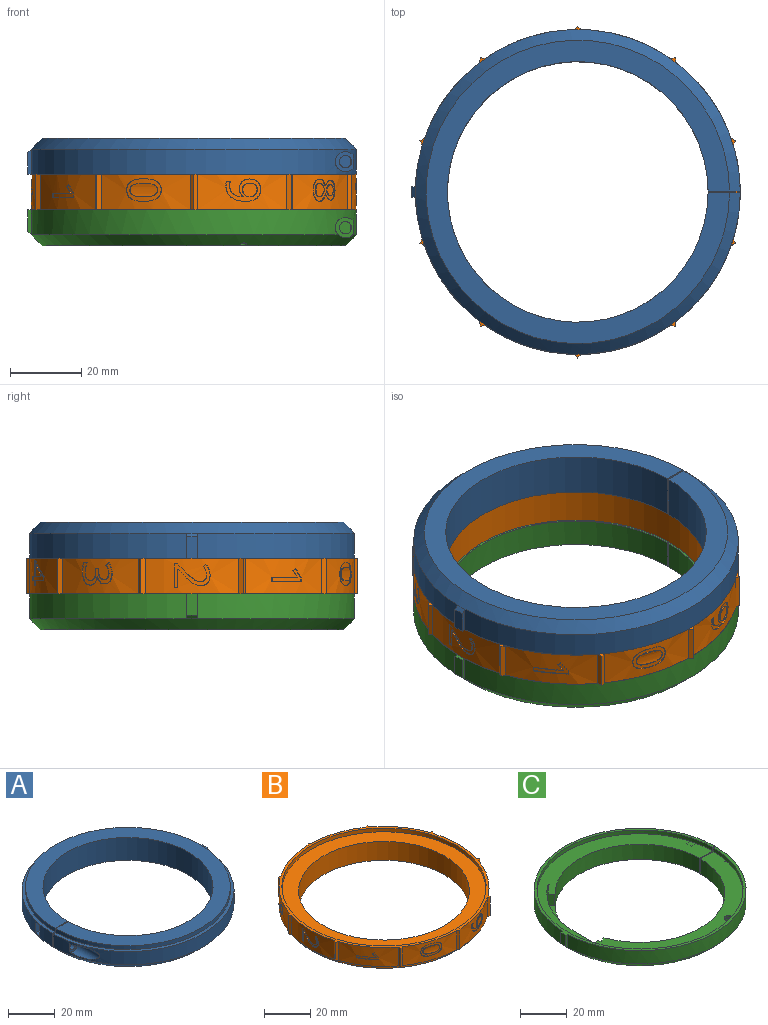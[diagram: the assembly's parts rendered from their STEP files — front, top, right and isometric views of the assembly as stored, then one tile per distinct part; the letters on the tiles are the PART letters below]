
ASSEMBLY  parts=3 mates=2
PART A: 26 faces, bbox 92x91x12 mm
  f0: plane 1.5x0.02mm, normal (0,0,-1), area 0mm2, adj f9,f23,f25
  f1: cylinder r=45.5mm len=90.97mm, axis (0,0,-1), area 970.8mm2, adj f5,f9,f11,f15,f16,f17,f18,f23
  f2: cylinder r=45.5mm len=90.97mm, axis (0,0,-1), area 920.2mm2, adj f5,f9,f10,f13,f14,f21
  f3: cylinder r=1.7mm len=8.75mm, axis (0,1,0), area 93.5mm2, adj f10,f14
  f4: cylinder r=36.5mm len=73mm, axis (0,0,-1), area 2746mm2, adj f6,f8,f10,f11
  f5: plane 92x91mm, normal (0,0,1), area 424mm2, adj f1,f2,f7,f10,f11,f21,f22,f23
  f6: plane 85x85mm, normal (0,0,-1), area 1486.1mm2, adj f4,f9,f10,f11
  f7: cylinder r=44mm len=88mm, axis (0,0,-1), area 551.9mm2, adj f5,f8,f10,f11
  f8: plane 88x88mm, normal (0,0,1), area 1893mm2, adj f4,f7,f10,f11
  f9: cone r=45.5mm half-angle=45deg, axis (0,0,1), area 1170.8mm2, adj f0,f1,f2,f6,f10,f11,f24
  f10: plane 12x9mm, normal (0,1,0), area 91.4mm2, adj f2,f3,f4,f5,f6,f7,f8,f9
  f11: plane 12x9mm, normal (0,-1,0), area 91.4mm2, adj f1,f4,f5,f6,f7,f8,f9,f12
  f12: cylinder r=1.7mm len=8.75mm, axis (0,1,0), area 93.5mm2, adj f11,f18
  f13: cylinder r=2.85mm len=13.32mm, axis (0,1,0), area 118.8mm2, adj f2,f14
  f14: plane 5.7x4.95mm, normal (0,-1,0), area 14.5mm2, adj f2,f3,f13
  f15: plane 3.75x3mm, normal (0,0,1), area 10.2mm2, adj f1,f17,f18,f19
  f16: plane 3.75x3mm, normal (0,0,-1), area 10.2mm2, adj f1,f17,f18,f20
  f17: plane 5.7x4.68mm, normal (0,-1,0), area 22mm2, adj f1,f15,f16,f19,f20
  f18: plane 5.7x5.39mm, normal (0,1,0), area 17mm2, adj f1,f12,f15,f16,f19,f20
  f19: plane 3x2.85mm, normal (-0.87,0,0.5), area 9.9mm2, adj f15,f17,f18,f20
  f20: plane 3x2.85mm, normal (-0.87,0,-0.5), area 9.9mm2, adj f16,f17,f18,f19
  f21: plane 7x1.02mm, normal (0,-1,0), area 6.7mm2, adj f2,f5,f22,f24,f25
  f22: plane 6x3mm, normal (1,0,0), area 18mm2, adj f5,f21,f23,f25
  f23: plane 7x1.02mm, normal (0,1,0), area 6.7mm2, adj f0,f1,f5,f22,f25
  f24: plane 1.5x0.02mm, normal (0,0,-1), area 0mm2, adj f9,f21,f25
  f25: plane 3x1mm, normal (0.71,0,-0.71), area 4.2mm2, adj f0,f21,f22,f23,f24
PART B: 250 faces, bbox 91x93x12 mm
  f0: cylinder r=1.5mm len=3mm, axis (0,0,-1), area 18.8mm2, adj f1,f32
  f1: plane 3x3mm, normal (0,0,-1), area 7.1mm2, adj f0
  f2: cylinder r=1.5mm len=3mm, axis (0,0,-1), area 18.8mm2, adj f3,f32
  f3: plane 3x3mm, normal (0,0,-1), area 7.1mm2, adj f2
  f4: cylinder r=1.5mm len=3mm, axis (0,0,-1), area 18.8mm2, adj f5,f32
  f5: plane 3x3mm, normal (0,0,-1), area 7.1mm2, adj f4
  f6: cylinder r=1.5mm len=3mm, axis (0,0,-1), area 18.8mm2, adj f7,f32
  f7: plane 3x3mm, normal (0,0,-1), area 7.1mm2, adj f6
  f8: cylinder r=1.5mm len=3mm, axis (0,0,-1), area 18.8mm2, adj f9,f32
  f9: plane 3x3mm, normal (0,0,-1), area 7.1mm2, adj f8
  f10: cylinder r=1.5mm len=3mm, axis (0,0,-1), area 18.8mm2, adj f11,f32
  f11: plane 3x3mm, normal (0,0,-1), area 7.1mm2, adj f10
  f12: cylinder r=1.5mm len=3mm, axis (0,0,-1), area 18.8mm2, adj f13,f32
  f13: plane 3x3mm, normal (0,0,-1), area 7.1mm2, adj f12
  f14: cylinder r=1.5mm len=3mm, axis (0,0,-1), area 18.8mm2, adj f15,f32
  f15: plane 3x3mm, normal (0,0,-1), area 7.1mm2, adj f14
  f16: cylinder r=1.5mm len=3mm, axis (0,0,-1), area 18.8mm2, adj f17,f32
  f17: plane 3x3mm, normal (0,0,-1), area 7.1mm2, adj f16
  f18: cylinder r=45.5mm len=26.21mm, axis (0,0,-1), area 247.6mm2, adj f29,f30,f220,f221,f222,f223,f224,f225
  f19: cylinder r=45.5mm len=21.21mm, axis (0,0,-1), area 225.9mm2, adj f29,f30,f201,f202,f203,f204,f205,f206
  f20: cylinder r=45.5mm len=24.93mm, axis (0,0,-1), area 243.7mm2, adj f29,f30,f178,f179,f180,f181,f182,f183
  f21: cylinder r=45.5mm len=24.93mm, axis (0,0,-1), area 231.8mm2, adj f29,f30,f162,f163,f164,f165,f166,f167
  f22: cylinder r=45.5mm len=21.21mm, axis (0,0,-1), area 242.3mm2, adj f29,f30,f135,f136,f137,f138,f139,f140
  f23: cylinder r=45.5mm len=26.21mm, axis (0,0,-1), area 244.2mm2, adj f29,f30,f114,f115,f116,f117,f118,f119
  f24: cylinder r=45.5mm len=21.21mm, axis (0,0,-1), area 251.4mm2, adj f29,f30,f104,f105,f106,f107,f108,f109
  f25: cylinder r=45.5mm len=24.93mm, axis (0,0,-1), area 214.8mm2, adj f29,f30,f93,f94,f95,f96,f100,f101
  f26: cylinder r=45.5mm len=21.21mm, axis (0,0,-1), area 223.1mm2, adj f29,f30,f67,f68,f69,f70,f71,f72
  f27: cylinder r=45.5mm len=24.93mm, axis (0,0,-1), area 225.9mm2, adj f29,f30,f40,f41,f42,f43,f44,f45
  f28: cylinder r=37mm len=74mm, axis (0,0,-1), area 2324.8mm2, adj f32,f34
  f29: plane 92.98x91mm, normal (0,0,1), area 362.3mm2, adj f18,f19,f20,f21,f22,f23,f24,f25
  f30: plane 92.98x91mm, normal (0,0,-1), area 431.6mm2, adj f18,f19,f20,f21,f22,f23,f24,f25
  f31: cylinder r=44mm len=88mm, axis (0,0,1), area 552.9mm2, adj f30,f32
  f32: plane 88x88mm, normal (0,0,-1), area 1710.6mm2, adj f0,f2,f4,f6,f8,f10,f12,f14
  f33: cylinder r=44.25mm len=88.5mm, axis (0,0,1), area 556.1mm2, adj f29,f34
  f34: plane 88.5x88.5mm, normal (0,0,1), area 1850.6mm2, adj f28,f33
  f35: extruded ~1.74x0.9mm, area 0.5mm2, adj f36,f53,f57,f58
  f36: extruded ~1.35x0.67mm, area 0.5mm2, adj f35,f37,f57,f58
  f37: extruded ~1.45x0.83mm, area 0.5mm2, adj f36,f38,f57,f58
  f38: extruded ~1.81x0.92mm, area 0.6mm2, adj f37,f39,f57,f58
  f39: extruded ~1.29x0.69mm, area 0.4mm2, adj f38,f52,f57,f58
  f40: extruded ~1.17x0.34mm, area 0.4mm2, adj f27,f41,f55,f57
  f41: extruded ~5.72x4.33mm, area 2.5mm2, adj f27,f40,f42,f57
  f42: extruded ~3.2x1.43mm, area 1mm2, adj f27,f41,f43,f57
  f43: extruded ~2.36x1.23mm, area 0.8mm2, adj f27,f42,f44,f57
  f44: extruded ~2.2x0.97mm, area 0.7mm2, adj f27,f43,f45,f57
  f45: extruded ~2.46x1.19mm, area 0.8mm2, adj f27,f44,f46,f57
  f46: extruded ~2.21x1mm, area 0.7mm2, adj f27,f45,f47,f57
  f47: extruded ~2.07x0.86mm, area 0.7mm2, adj f27,f46,f48,f57
  f48: extruded ~2.09x1.2mm, area 0.8mm2, adj f27,f47,f49,f57
  f49: plane 0.29x0.09mm, normal (0.95,0.31,0), area 0mm2, adj f27,f48,f50,f57
  f50: extruded ~3.01x1.33mm, area 1mm2, adj f27,f49,f51,f57
  f51: extruded ~2.28x1.03mm, area 0.8mm2, adj f27,f50,f56,f57
  f52: extruded ~1.45x0.62mm, area 0.5mm2, adj f39,f54,f57,f58
  f53: extruded ~1.54x0.78mm, area 0.5mm2, adj f35,f54,f57,f58
  f54: extruded ~1.33x0.6mm, area 0.4mm2, adj f52,f53,f57,f58
  f55: plane 1.13x0.51mm, normal (0,0,-1), area 0.3mm2, adj f27,f40,f56,f57
  f56: extruded ~1.13x0.35mm, area 0.3mm2, adj f27,f51,f55,f57
  f57: cylinder r=45.5mm len=9.7mm, axis (0,0,-1), area 26.6mm2, adj f35,f36,f37,f38,f39,f40,f41,f42
  f58: cylinder r=45.5mm len=4.07mm, axis (0,0,-1), area 12mm2, adj f35,f36,f37,f38,f39,f52,f53,f54
  f59: plane 0.26x0.22mm, normal (0.53,0.73,-0.43), area 0.1mm2, adj f60,f79,f85,f86
  f60: extruded ~1.45x0.94mm, area 0.4mm2, adj f59,f61,f85,f86
  f61: extruded ~1.05x0.88mm, area 0.3mm2, adj f60,f62,f85,f86
  f62: extruded ~1.2x1mm, area 0.3mm2, adj f61,f78,f85,f86
  f63: extruded ~1.26x0.85mm, area 0.4mm2, adj f64,f83,f85,f87
  f64: extruded ~1.01x0.85mm, area 0.3mm2, adj f63,f65,f85,f87
  f65: extruded ~1.03x0.87mm, area 0.3mm2, adj f64,f66,f85,f87
  f66: extruded ~1.14x0.46mm, area 0.3mm2, adj f65,f76,f85,f87
  f67: extruded ~2.16x1.78mm, area 0.8mm2, adj f26,f68,f81,f85
  f68: extruded ~1.64x1.34mm, area 0.5mm2, adj f26,f67,f69,f85
  f69: extruded ~2.02x0.71mm, area 0.5mm2, adj f26,f68,f70,f85
  f70: extruded ~2x0.71mm, area 0.5mm2, adj f26,f69,f71,f85
  f71: extruded ~1.63x1.33mm, area 0.5mm2, adj f26,f70,f72,f85
  f72: extruded ~2.22x1.74mm, area 0.8mm2, adj f26,f71,f73,f85
  f73: extruded ~2.34x1.91mm, area 0.9mm2, adj f26,f72,f74,f85
  f74: extruded ~1.82x1.48mm, area 0.6mm2, adj f26,f73,f75,f85
  f75: extruded ~2.29x0.76mm, area 0.6mm2, adj f26,f74,f77,f85
  f76: extruded ~1.17x0.46mm, area 0.3mm2, adj f66,f84,f85,f87
  f77: extruded ~2.26x0.8mm, area 0.6mm2, adj f26,f75,f82,f85
  f78: extruded ~1.43x0.53mm, area 0.4mm2, adj f62,f80,f85,f86
  f79: extruded ~1.97x1.72mm, area 0.7mm2, adj f59,f80,f85,f86
  f80: extruded ~1.87x1.53mm, area 0.7mm2, adj f78,f79,f85,f86
  f81: extruded ~2.34x2.09mm, area 0.9mm2, adj f26,f67,f82,f85
  f82: extruded ~1.83x1.48mm, area 0.6mm2, adj f26,f77,f81,f85
  f83: extruded ~1.71x1.57mm, area 0.7mm2, adj f63,f84,f85,f87
  f84: extruded ~1.03x0.87mm, area 0.3mm2, adj f76,f83,f85,f87
  f85: cylinder r=45.5mm len=8.25mm, axis (0,0,-1), area 30.7mm2, adj f59,f60,f61,f62,f63,f64,f65,f66
  f86: cylinder r=45.5mm len=3.8mm, axis (0,0,-1), area 10.9mm2, adj f59,f60,f61,f62,f78,f79,f80
  f87: cylinder r=45.5mm len=3.17mm, axis (0,0,-1), area 6.8mm2, adj f63,f64,f65,f66,f76,f83,f84
  f88: extruded ~1.44x1mm, area 0.5mm2, adj f89,f98,f102,f103
  f89: extruded ~3.07x1.3mm, area 0.8mm2, adj f88,f90,f102,f103
  f90: extruded ~3.05x1.29mm, area 0.8mm2, adj f89,f91,f102,f103
  f91: extruded ~1.44x1mm, area 0.5mm2, adj f90,f92,f102,f103
  f92: extruded ~1.46x1.01mm, area 0.5mm2, adj f91,f97,f102,f103
  f93: extruded ~5.03x3.18mm, area 1.7mm2, adj f25,f94,f100,f102
  f94: extruded ~3.73x1.56mm, area 1mm2, adj f25,f93,f95,f102
  f95: extruded ~2.38x1.37mm, area 0.7mm2, adj f25,f94,f96,f102
  f96: extruded ~5.02x3.16mm, area 1.7mm2, adj f25,f95,f101,f102
  f97: extruded ~3.05x1.29mm, area 0.8mm2, adj f92,f99,f102,f103
  f98: extruded ~1.46x1.01mm, area 0.5mm2, adj f88,f99,f102,f103
  f99: extruded ~3.06x1.3mm, area 0.8mm2, adj f97,f98,f102,f103
  f100: extruded ~2.35x1.37mm, area 0.7mm2, adj f25,f93,f101,f102
  f101: extruded ~3.74x1.56mm, area 1mm2, adj f25,f96,f100,f102
  f102: cylinder r=45.5mm len=9.71mm, axis (0,0,-1), area 27.5mm2, adj f88,f89,f90,f91,f92,f93,f94,f95
  f103: cylinder r=45.5mm len=7.7mm, axis (0,0,-1), area 23.7mm2, adj f88,f89,f90,f91,f92,f97,f98,f99
  f104: plane 1.19x0.2mm, normal (0.59,-0.81,0), area 0.3mm2, adj f24,f105,f111,f113
  f105: plane 8.17x6.02mm, normal (0,0,1), area 2.5mm2, adj f24,f104,f106,f113
  f106: plane 1.02x0.2mm, normal (-0.59,0.81,0), area 0.3mm2, adj f24,f105,f112,f113
  f107: plane 0.79x0.73mm, normal (0.36,-0.5,-0.79), area 0.3mm2, adj f24,f108,f112,f113
  f108: plane 1x0.78mm, normal (0.45,-0.63,0.63), area 0.3mm2, adj f24,f107,f109,f113
  f109: extruded ~0.82x0.8mm, area 0.3mm2, adj f24,f108,f110,f113
  f110: extruded ~2.2x1.75mm, area 0.6mm2, adj f24,f109,f111,f113
  f111: plane 5.31x3.63mm, normal (0,0,-1), area 1.5mm2, adj f24,f104,f110,f113
  f112: plane 2.6x1.69mm, normal (-0.46,0.64,-0.62), area 0.8mm2, adj f24,f106,f107,f113
  f113: cylinder r=45.5mm len=8.03mm, axis (0,0,-1), area 14.5mm2, adj f104,f105,f106,f107,f108,f109,f110,f111
  f114: plane 1.04x0.35mm, normal (0,0,1), area 0.3mm2, adj f23,f115,f132,f134
  f115: plane 5.1x0.25mm, normal (0,1,0), area 1.3mm2, adj f23,f114,f116,f134
  f116: plane 0.25x0.05mm, normal (0,0,1), area 0mm2, adj f23,f115,f117,f134
  f117: plane 2.17x2.12mm, normal (0,-0.71,0.7), area 0.8mm2, adj f23,f116,f118,f134
  f118: extruded ~2.33x1.98mm, area 0.8mm2, adj f23,f117,f119,f134
  f119: extruded ~1.87x0.53mm, area 0.5mm2, adj f23,f118,f120,f134
  f120: extruded ~1.92x0.79mm, area 0.5mm2, adj f23,f119,f121,f134
  f121: extruded ~2.19x0.72mm, area 0.6mm2, adj f23,f120,f122,f134
  f122: extruded ~2.98x1.14mm, area 0.8mm2, adj f23,f121,f123,f134
  f123: plane 0.77x0.6mm, normal (0,-0.61,-0.79), area 0.2mm2, adj f23,f122,f124,f134
  f124: extruded ~1.23x0.74mm, area 0.4mm2, adj f23,f123,f125,f134
  f125: extruded ~1.17x0.27mm, area 0.3mm2, adj f23,f124,f126,f134
  f126: extruded ~1.34x0.46mm, area 0.4mm2, adj f23,f125,f127,f134
  f127: extruded ~1.26x0.48mm, area 0.3mm2, adj f23,f126,f128,f134
  f128: extruded ~1.05x0.29mm, area 0.3mm2, adj f23,f127,f129,f134
  f129: extruded ~1x0.57mm, area 0.3mm2, adj f23,f128,f130,f134
  f130: extruded ~1.72x1.57mm, area 0.6mm2, adj f23,f129,f131,f134
  f131: plane 2.63x2.61mm, normal (0,0.71,-0.71), area 0.9mm2, adj f23,f130,f133,f134
  f132: plane 6.52x0.25mm, normal (0,-1,0), area 1.6mm2, adj f23,f114,f133,f134
  f133: plane 0.97x0.35mm, normal (0,0,-1), area 0.2mm2, adj f23,f131,f132,f134
  f134: cylinder r=45.5mm len=10.06mm, axis (0,0,-1), area 21.7mm2, adj f114,f115,f116,f117,f118,f119,f120,f121
  f135: extruded ~1.59x0.81mm, area 0.5mm2, adj f22,f136,f156,f158
  f136: extruded ~1.45x1.17mm, area 0.4mm2, adj f22,f135,f137,f158
  f137: extruded ~1.68x1.37mm, area 0.5mm2, adj f22,f136,f138,f158
  f138: extruded ~2.18x0.73mm, area 0.6mm2, adj f22,f137,f139,f158
  f139: extruded ~2.96x1.03mm, area 0.8mm2, adj f22,f138,f140,f158
  f140: plane 0.87x0.65mm, normal (-0.35,-0.48,-0.81), area 0.3mm2, adj f22,f139,f141,f158
  f141: extruded ~2.33x0.85mm, area 0.6mm2, adj f22,f140,f142,f158
  f142: extruded ~1.23x0.49mm, area 0.3mm2, adj f22,f141,f143,f158
  f143: extruded ~1.08x0.91mm, area 0.3mm2, adj f22,f142,f144,f158
  f144: extruded ~1.28x1.05mm, area 0.4mm2, adj f22,f143,f145,f158
  f145: extruded ~1.68x0.57mm, area 0.4mm2, adj f22,f144,f146,f158
  f146: plane 0.9x0.2mm, normal (0.59,0.81,0), area 0.2mm2, adj f22,f145,f147,f158
  f147: plane 0.98x0.8mm, normal (0,0,-1), area 0.3mm2, adj f22,f146,f148,f158
  f148: plane 0.9x0.2mm, normal (-0.59,-0.81,0), area 0.2mm2, adj f22,f147,f149,f158
  f149: extruded ~2.58x1.59mm, area 0.9mm2, adj f22,f148,f150,f158
  f150: extruded ~2.4x1.81mm, area 0.9mm2, adj f22,f149,f151,f158
  f151: extruded ~2.6x0.71mm, area 0.7mm2, adj f22,f150,f152,f158
  f152: plane 1.02x0.96mm, normal (0,0,-1), area 0.3mm2, adj f22,f151,f153,f158
  f153: extruded ~2.63x0.61mm, area 0.7mm2, adj f22,f152,f154,f158
  f154: extruded ~2.71x0.84mm, area 0.7mm2, adj f22,f153,f155,f158
  f155: extruded ~1.99x1.6mm, area 0.6mm2, adj f22,f154,f157,f158
  f156: plane 0.23x0.18mm, normal (0,0,1), area 0mm2, adj f22,f135,f157,f158
  f157: extruded ~2.45x2.09mm, area 0.9mm2, adj f22,f155,f156,f158
  f158: cylinder r=45.5mm len=8.24mm, axis (0,0,-1), area 23.6mm2, adj f135,f136,f137,f138,f139,f140,f141,f142
  f159: plane 3.37x0.24mm, normal (0.95,0.31,0), area 0.8mm2, adj f160,f172,f176,f177
  f160: plane 3.99x2.79mm, normal (-0.53,-0.17,0.83), area 1.2mm2, adj f159,f161,f176,f177
  f161: extruded ~1.26x0.69mm, area 0.3mm2, adj f160,f171,f176,f177
  f162: plane 1.17x0.53mm, normal (0,0,1), area 0.3mm2, adj f21,f163,f174,f176
  f163: plane 1.45x0.24mm, normal (0.95,0.31,0), area 0.4mm2, adj f21,f162,f164,f176
  f164: plane 6.3x2.51mm, normal (0,0,1), area 1.7mm2, adj f21,f163,f165,f176
  f165: plane 1.27x0.24mm, normal (0.95,0.31,0), area 0.3mm2, adj f21,f164,f166,f176
  f166: plane 6.35x4.51mm, normal (0.53,0.17,-0.83), area 2mm2, adj f21,f165,f167,f176
  f167: plane 1.12x0.52mm, normal (0,0,-1), area 0.3mm2, adj f21,f166,f168,f176
  f168: plane 4.58x0.24mm, normal (-0.95,-0.31,0), area 1.1mm2, adj f21,f167,f169,f176
  f169: plane 2.25x0.74mm, normal (0,0,-1), area 0.6mm2, adj f21,f168,f170,f176
  f170: plane 1.19x0.24mm, normal (-0.95,-0.31,0), area 0.3mm2, adj f21,f169,f175,f176
  f171: plane 0.24x0.08mm, normal (-0.95,-0.31,0), area 0mm2, adj f161,f173,f176,f177
  f172: plane 2.38x0.96mm, normal (0,0,-1), area 0.6mm2, adj f159,f173,f176,f177
  f173: extruded ~2.91x1.28mm, area 0.7mm2, adj f171,f172,f176,f177
  f174: plane 1.45x0.24mm, normal (-0.95,-0.31,0), area 0.4mm2, adj f21,f162,f175,f176
  f175: plane 2.25x0.74mm, normal (0,0,1), area 0.6mm2, adj f21,f170,f174,f176
  f176: cylinder r=45.5mm len=9.48mm, axis (0,0,-1), area 25.5mm2, adj f159,f160,f161,f162,f163,f164,f165,f166
  f177: cylinder r=45.5mm len=5.04mm, axis (0,0,-1), area 8.6mm2, adj f159,f160,f161,f171,f172,f173
  f178: extruded ~2.41x0.61mm, area 0.6mm2, adj f20,f179,f193,f195
  f179: extruded ~2.64x0.93mm, area 0.7mm2, adj f20,f178,f180,f195
  f180: extruded ~2.46x1.15mm, area 0.7mm2, adj f20,f179,f181,f195
  f181: extruded ~2.11x0.93mm, area 0.6mm2, adj f20,f180,f182,f195
  f182: extruded ~2.3x0.82mm, area 0.6mm2, adj f20,f181,f183,f195
  f183: extruded ~1.42x0.28mm, area 0.4mm2, adj f20,f182,f184,f195
  f184: plane 2.82x0.97mm, normal (-0.09,0.03,1), area 0.7mm2, adj f20,f183,f185,f195
  f185: plane 3.61x0.24mm, normal (-0.95,0.31,0), area 0.9mm2, adj f20,f184,f186,f195
  f186: plane 1.18x0.48mm, normal (0,0,1), area 0.3mm2, adj f20,f185,f187,f195
  f187: plane 4.68x0.24mm, normal (0.95,-0.31,0), area 1.2mm2, adj f20,f186,f188,f195
  f188: plane 4.6x1.43mm, normal (0.08,-0.02,-1), area 1.2mm2, adj f20,f187,f189,f195
  f189: plane 0.61x0.44mm, normal (-0.8,0.26,-0.53), area 0.2mm2, adj f20,f188,f190,f195
  f190: extruded ~1.57x0.29mm, area 0.4mm2, adj f20,f189,f191,f195
  f191: extruded ~2.33x1.99mm, area 0.9mm2, adj f20,f190,f192,f195
  f192: extruded ~2.28x2.15mm, area 0.9mm2, adj f20,f191,f194,f195
  f193: plane 1.16x0.7mm, normal (0,0,-1), area 0.3mm2, adj f20,f178,f194,f195
  f194: extruded ~2.44x0.71mm, area 0.6mm2, adj f20,f192,f193,f195
  f195: cylinder r=45.5mm len=9.55mm, axis (0,0,-1), area 22.2mm2, adj f178,f179,f180,f181,f182,f183,f184,f185
  f196: extruded ~1.58x1.28mm, area 0.4mm2, adj f197,f214,f218,f219
  f197: extruded ~1.35x0.66mm, area 0.4mm2, adj f196,f198,f218,f219
  f198: extruded ~1.44x0.79mm, area 0.4mm2, adj f197,f199,f218,f219
  f199: extruded ~1.64x1.33mm, area 0.5mm2, adj f198,f200,f218,f219
  f200: extruded ~1.18x0.96mm, area 0.4mm2, adj f199,f213,f218,f219
  f201: extruded ~1.17x0.29mm, area 0.3mm2, adj f19,f202,f216,f218
  f202: extruded ~5.02x4.33mm, area 2.1mm2, adj f19,f201,f203,f218
  f203: extruded ~2.86x2.24mm, area 0.9mm2, adj f19,f202,f204,f218
  f204: extruded ~2.36x1.14mm, area 0.7mm2, adj f19,f203,f205,f218
  f205: extruded ~2.19x0.92mm, area 0.6mm2, adj f19,f204,f206,f218
  f206: extruded ~2.22x1.77mm, area 0.7mm2, adj f19,f205,f207,f218
  f207: extruded ~1.95x1.53mm, area 0.6mm2, adj f19,f206,f208,f218
  f208: extruded ~2.07x0.81mm, area 0.6mm2, adj f19,f207,f209,f218
  f209: extruded ~2.08x1.09mm, area 0.6mm2, adj f19,f208,f210,f218
  f210: plane 0.2x0.15mm, normal (0.59,-0.81,0), area 0mm2, adj f19,f209,f211,f218
  f211: extruded ~2.66x2.07mm, area 0.8mm2, adj f19,f210,f212,f218
  f212: extruded ~2.28x0.97mm, area 0.6mm2, adj f19,f211,f217,f218
  f213: extruded ~1.44x0.59mm, area 0.4mm2, adj f200,f215,f218,f219
  f214: extruded ~1.39x1.12mm, area 0.4mm2, adj f196,f215,f218,f219
  f215: extruded ~1.33x0.58mm, area 0.4mm2, adj f213,f214,f218,f219
  f216: plane 0.94x0.9mm, normal (0,0,1), area 0.3mm2, adj f19,f201,f217,f218
  f217: extruded ~1.13x0.31mm, area 0.3mm2, adj f19,f212,f216,f218
  f218: cylinder r=45.5mm len=8.25mm, axis (0,0,-1), area 26.7mm2, adj f196,f197,f198,f199,f200,f201,f202,f203
  f219: cylinder r=45.5mm len=3.82mm, axis (0,0,-1), area 12mm2, adj f196,f197,f198,f199,f200,f213,f214,f215
  f220: plane 1.32x0.25mm, normal (0,1,0), area 0.3mm2, adj f18,f221,f225,f227
  f221: plane 8.94x3.77mm, normal (0,0.39,0.92), area 2.4mm2, adj f18,f220,f226,f227
  f222: plane 6.37x0.25mm, normal (0,-1,0), area 1.6mm2, adj f18,f223,f226,f227
  f223: plane 1.13x0.36mm, normal (0,0,-1), area 0.3mm2, adj f18,f222,f224,f227
  f224: plane 5.11x0.25mm, normal (0,1,0), area 1.3mm2, adj f18,f223,f225,f227
  f225: plane 8.79x3.82mm, normal (0,-0.4,-0.92), area 2.4mm2, adj f18,f220,f224,f227
  f226: plane 0.98x0.35mm, normal (0,0,1), area 0.2mm2, adj f18,f221,f222,f227
  f227: cylinder r=45.5mm len=9.92mm, axis (0,0,-1), area 18.3mm2, adj f220,f221,f222,f223,f224,f225,f226
  f228: plane 10x1mm, normal (-0.71,0.71,0), area 14.1mm2, adj f21,f29,f30,f229
  f229: plane 10x1mm, normal (0.71,0.71,0), area 14.1mm2, adj f20,f29,f30,f228
  f230: plane 10x1.4mm, normal (-0.99,0.16,0), area 14.1mm2, adj f22,f29,f30,f231
  f231: plane 10x1.4mm, normal (0.16,0.99,0), area 14.1mm2, adj f21,f29,f30,f230
  f232: plane 10x1.26mm, normal (-0.89,-0.45,0), area 14.1mm2, adj f23,f29,f30,f233
  f233: plane 10x1.26mm, normal (-0.45,0.89,0), area 14.1mm2, adj f22,f29,f30,f232
  f234: plane 10x1.26mm, normal (-0.45,-0.89,0), area 14.1mm2, adj f24,f29,f30,f235
  f235: plane 10x1.26mm, normal (-0.89,0.45,0), area 14.1mm2, adj f23,f29,f30,f234
  f236: plane 10x1.4mm, normal (0.16,-0.99,0), area 14.1mm2, adj f25,f29,f30,f237
  f237: plane 10x1.4mm, normal (-0.99,-0.16,0), area 14.1mm2, adj f24,f29,f30,f236
  f238: plane 10x1mm, normal (0.71,-0.71,0), area 14.1mm2, adj f27,f29,f30,f239
  f239: plane 10x1mm, normal (-0.71,-0.71,0), area 14.1mm2, adj f25,f29,f30,f238
  f240: plane 10x1.4mm, normal (0.99,-0.16,0), area 14.1mm2, adj f26,f29,f30,f241
  f241: plane 10x1.4mm, normal (-0.16,-0.99,0), area 14.1mm2, adj f27,f29,f30,f240
  f242: plane 10x1.26mm, normal (0.89,0.45,0), area 14.1mm2, adj f18,f29,f30,f243
  f243: plane 10x1.26mm, normal (0.45,-0.89,0), area 14.1mm2, adj f26,f29,f30,f242
  f244: plane 10x1.26mm, normal (0.45,0.89,0), area 14.1mm2, adj f19,f29,f30,f245
  f245: plane 10x1.26mm, normal (0.89,-0.45,0), area 14.1mm2, adj f18,f29,f30,f244
  f246: plane 10x1.4mm, normal (-0.16,0.99,0), area 14.1mm2, adj f20,f29,f30,f247
  f247: plane 10x1.4mm, normal (0.99,0.16,0), area 14.1mm2, adj f19,f29,f30,f246
  f248: cylinder r=1.5mm len=3mm, axis (0,0,-1), area 18.8mm2, adj f32,f249
  f249: plane 3x3mm, normal (0,0,-1), area 7.1mm2, adj f248
PART C: 42 faces, bbox 92x91x10 mm
  f0: cylinder r=45.5mm len=90.97mm, axis (0,0,-1), area 974.7mm2, adj f1,f8,f26,f27,f32,f35,f40
  f1: cone r=45.5mm half-angle=45deg, axis (0,0,1), area 1155.1mm2, adj f0,f2,f3,f9,f22,f26,f27,f31
  f2: plane 1.5x0.02mm, normal (0,0,-1), area 0mm2, adj f1,f37,f39
  f3: cylinder r=45.5mm len=90.97mm, axis (0,0,-1), area 926.5mm2, adj f1,f8,f22,f23,f33,f37
  f4: plane 45.99x17.02mm, normal (0,0,1), area 159.5mm2, adj f5,f7,f12,f13,f14,f19,f20,f21
  f5: cylinder r=39.5mm len=6mm, axis (0,0,1), area 9.2mm2, adj f4,f6,f13,f34
  f6: plane 88.5x88.5mm, normal (0,0,1), area 1791.4mm2, adj f5,f7,f10,f12,f13,f14,f15,f19
  f7: cylinder r=36.5mm len=73mm, axis (0,0,-1), area 1586.4mm2, adj f4,f6,f9,f21,f32,f33,f34
  f8: plane 92x91mm, normal (0,0,1), area 354.8mm2, adj f0,f3,f10,f32,f33,f35,f36,f37
  f9: plane 85x85mm, normal (0,0,-1), area 1484.1mm2, adj f1,f7,f32,f33,f41
  f10: cylinder r=44.25mm len=88.5mm, axis (0,0,1), area 555.1mm2, adj f6,f8,f32,f33
  f11: cylinder r=1.7mm len=8.75mm, axis (0,-1,0), area 93.5mm2, adj f23,f33
  f12: plane 12x6mm, normal (1,0,0), area 72mm2, adj f4,f6,f13,f14
  f13: plane 6x2.37mm, normal (0,1,0), area 14.2mm2, adj f4,f5,f6,f12
  f14: cylinder r=40mm len=32.54mm, axis (0,0,1), area 228mm2, adj f4,f6,f12,f19
  f15: cylinder r=1.9mm len=3.8mm, axis (0,0,1), area 11.9mm2, adj f6,f16
  f16: plane 3.8x3.8mm, normal (0,0,1), area 3.8mm2, adj f15,f18
  f17: plane 3.1x3.1mm, normal (0,0,1), area 4.4mm2, adj f18,f41
  f18: cylinder r=1.55mm len=3.2mm, axis (0,0,1), area 31.2mm2, adj f16,f17
  f19: plane 6x0.41mm, normal (-0.81,-0.58,0), area 3mm2, adj f4,f6,f14,f20
  f20: cylinder r=39.5mm len=6mm, axis (0,0,1), area 43.1mm2, adj f4,f6,f19,f21
  f21: plane 6x2.16mm, normal (-0.69,-0.72,0), area 18mm2, adj f4,f6,f7,f20
  f22: cylinder r=2.85mm len=13.32mm, axis (0,1,0), area 110.8mm2, adj f1,f3,f23
  f23: plane 5.7x4.95mm, normal (0,-1,0), area 14.5mm2, adj f3,f11,f22
  f24: cylinder r=1.7mm len=8.75mm, axis (0,-1,0), area 93.5mm2, adj f27,f32
  f25: plane 3x0.42mm, normal (-0.87,0,-0.5), area 1.5mm2, adj f26,f27,f28,f40
  f26: plane 5.7x5.18mm, normal (0,-1,0), area 24.4mm2, adj f0,f1,f25,f28,f29,f30,f31
  f27: plane 5.89x5.7mm, normal (0,1,0), area 19.1mm2, adj f0,f1,f24,f25,f28,f29,f30,f31
  f28: plane 3.29x3mm, normal (0,0,-1), area 9.9mm2, adj f25,f26,f27,f29
  f29: plane 3x2.85mm, normal (0.87,0,-0.5), area 9.9mm2, adj f26,f27,f28,f30
  f30: plane 3x2.85mm, normal (0.87,0,0.5), area 9.9mm2, adj f26,f27,f29,f31
  f31: plane 3.38x3mm, normal (0,0,1), area 9.1mm2, adj f1,f26,f27,f30
  f32: plane 10x9mm, normal (0,-1,0), area 60.9mm2, adj f0,f1,f6,f7,f8,f9,f10,f24
  f33: plane 10x9mm, normal (0,1,0), area 60.9mm2, adj f1,f3,f6,f7,f8,f9,f10,f11
  f34: plane 6x2.82mm, normal (-0.34,0.94,0), area 18mm2, adj f4,f5,f6,f7
  f35: plane 7x1.02mm, normal (0,1,0), area 6.7mm2, adj f0,f8,f36,f38,f39
  f36: plane 6x3mm, normal (-1,0,0), area 18mm2, adj f8,f35,f37,f39
  f37: plane 7x1.02mm, normal (0,-1,0), area 6.7mm2, adj f2,f3,f8,f36,f39
  f38: plane 1.5x0.02mm, normal (0,0,-1), area 0mm2, adj f1,f35,f39
  f39: plane 3x1mm, normal (-0.71,0,-0.71), area 4.2mm2, adj f2,f35,f36,f37,f38
  f40: plane 3x0.71mm, normal (0,0,-1), area 1.1mm2, adj f0,f25,f27
  f41: cylinder r=1mm len=3.8mm, axis (0,0,1), area 22.6mm2, adj f1,f9,f17
PLACE A rot(axis=(0,1,0),180deg) t=(-9.1,-6.33,9.39)mm
PLACE B t=(-9.1,-6.33,-5.61)mm fixed
PLACE C t=(-9.1,-6.33,-10.61)mm
MATE fastened C.f10 <-> B.f31  axis (0,0,1) through (-9.1,-6.33,-6.61)mm
MATE fastened A.f1 <-> C.f0  axis (0,0,1) through (-9.1,-6.33,7.89)mm
